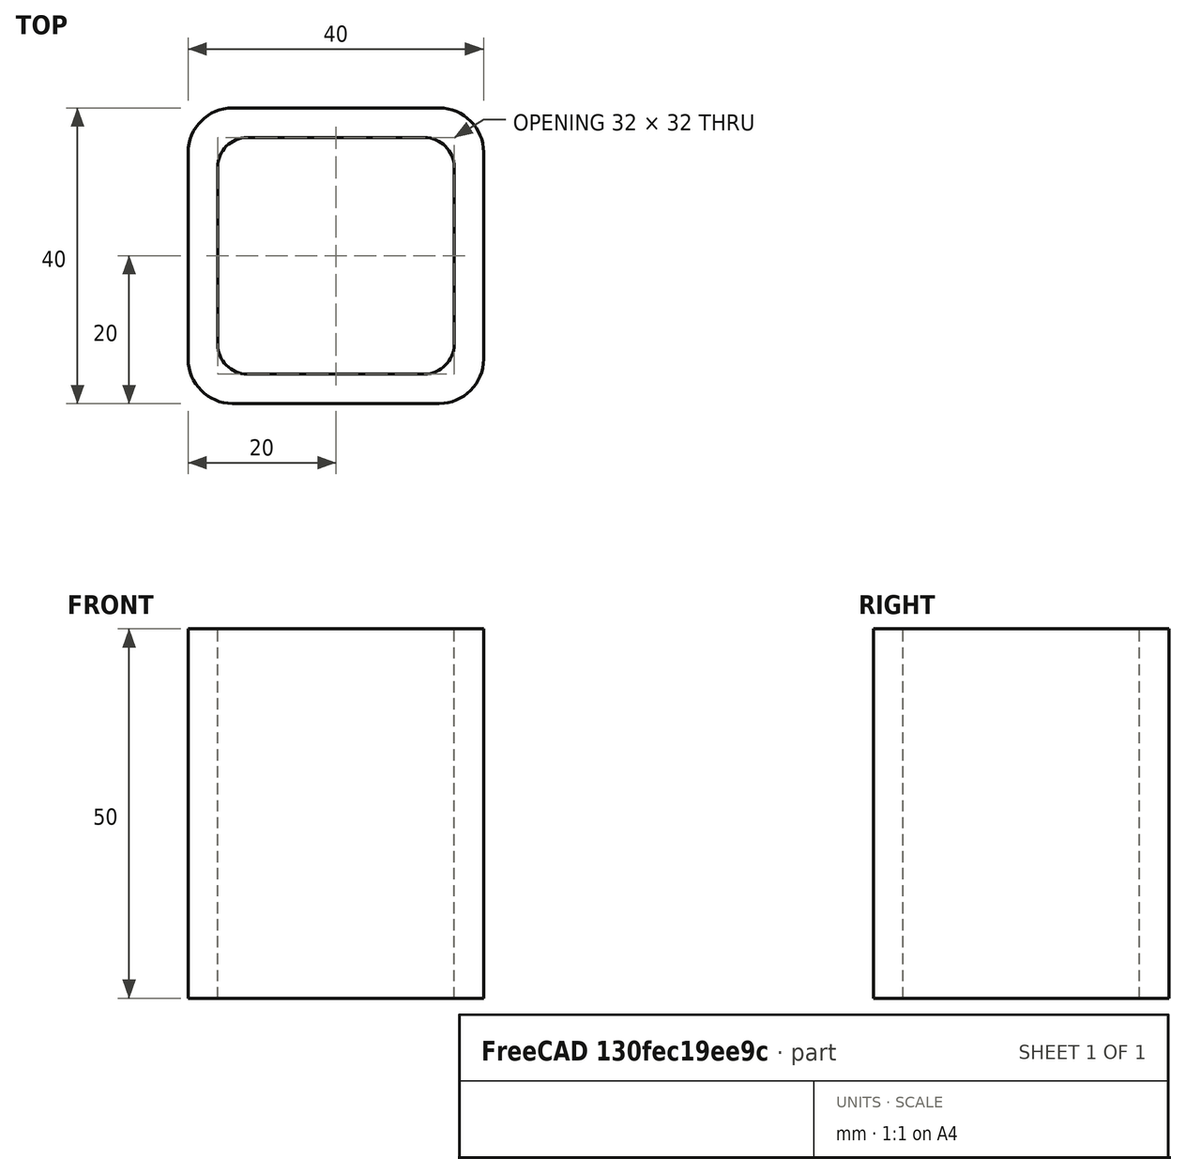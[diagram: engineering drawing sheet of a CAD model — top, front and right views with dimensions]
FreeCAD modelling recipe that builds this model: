
FCSTD DOCUMENT  (FreeCAD 0.15R4671 (Git))
Label: Square hollow section 40x40x4 EN10219 S235JRH
License: All rights reserved
LicenseURL: http://en.wikipedia.org/wiki/All_rights_reserved
objects: Sketcher::SketchObject×1, Part::Extrusion×1
note: 2 computed .brp shape members not serialized (recipe doc carries the construction recipe); baked Part::Feature solids carry a one-line shape summary decoded from their .brp

FEATURE [Sketcher::SketchObject] Sketch
  sketch-geometry (16):
    g0: LineSegment StartX=-12 StartY=16 StartZ=0 EndX=12 EndY=16 EndZ=0
    g1: LineSegment StartX=16 StartY=12 StartZ=0 EndX=16 EndY=-12 EndZ=0
    g2: LineSegment StartX=12 StartY=-16 StartZ=0 EndX=-12 EndY=-16 EndZ=0
    g3: LineSegment StartX=-16 StartY=-12 StartZ=0 EndX=-16 EndY=12 EndZ=0
    g4: LineSegment StartX=-14 StartY=20 StartZ=0 EndX=14 EndY=20 EndZ=0
    g5: LineSegment StartX=20 StartY=14 StartZ=0 EndX=20 EndY=-14 EndZ=0
    g6: LineSegment StartX=14 StartY=-20 StartZ=0 EndX=-14 EndY=-20 EndZ=0
    g7: LineSegment StartX=-20 StartY=-14 StartZ=0 EndX=-20 EndY=14 EndZ=0
    g8: ArcOfCircle CenterX=-12 CenterY=12 CenterZ=0 NormalX=0 NormalY=0 NormalZ=1 Radius=4 StartAngle=1.5708 EndAngle=3.14159
    g9: ArcOfCircle CenterX=12 CenterY=12 CenterZ=0 NormalX=0 NormalY=0 NormalZ=1 Radius=4 StartAngle=0 EndAngle=1.5708
    g10: ArcOfCircle CenterX=12 CenterY=-12 CenterZ=0 NormalX=0 NormalY=0 NormalZ=1 Radius=4 StartAngle=4.71239 EndAngle=6.28319
    g11: ArcOfCircle CenterX=-12 CenterY=-12 CenterZ=0 NormalX=0 NormalY=0 NormalZ=1 Radius=4 StartAngle=3.14159 EndAngle=4.71239
    g12: ArcOfCircle CenterX=14 CenterY=14 CenterZ=0 NormalX=0 NormalY=0 NormalZ=1 Radius=6 StartAngle=0 EndAngle=1.5708
    g13: ArcOfCircle CenterX=14 CenterY=-14 CenterZ=0 NormalX=0 NormalY=0 NormalZ=1 Radius=6 StartAngle=4.71239 EndAngle=6.28319
    g14: ArcOfCircle CenterX=-14 CenterY=-14 CenterZ=0 NormalX=0 NormalY=0 NormalZ=1 Radius=6 StartAngle=3.14159 EndAngle=4.71239
    g15: ArcOfCircle CenterX=-14 CenterY=14 CenterZ=0 NormalX=0 NormalY=0 NormalZ=1 Radius=6 StartAngle=1.5708 EndAngle=3.14159
  constraints (36):
    c: Horizontal(g2)
    c: Vertical(g3)
    c: Horizontal(g6)
    c: Vertical(g7)
    c: Tangent(g3,g8) = 1.5708
    c: Tangent(g0,g8) = 1.5708
    c: Tangent(g0,g9) = 1.5708
    c: Tangent(g1,g9) = 1.5708
    c: Tangent(g1,g10) = 1.5708
    c: Tangent(g2,g10) = 1.5708
    c: Tangent(g2,g11) = 1.5708
    c: Tangent(g3,g11) = 1.5708
    c: Tangent(g4,g12) = 1.5708
    c: Tangent(g5,g12) = 1.5708
    c: Tangent(g5,g13) = 1.5708
    c: Tangent(g6,g13) = 1.5708
    c: Tangent(g6,g14) = 1.5708
    c: Tangent(g7,g14) = 1.5708
    c: Tangent(g7,g15) = 1.5708
    c: Tangent(g4,g15) = 1.5708
    c: Equal(g9,g8)
    c: Equal(g9,g11)
    c: Equal(g9,g10)
    c: Equal(g12,g15)
    c: Equal(g12,g14)
    c: Equal(g12,g13)
    c: Symmetric(g4,g6,g-1)
    c: Symmetric(g7,g5,g-2)
    c: DistanceY(g4,g6) = -40
    c: DistanceX(g7,g5) = 40
    c: Symmetric(g3,g1,g-2)
    c: Symmetric(g0,g2,g-1)
    c: DistanceY(g0,g4) = 4
    c: DistanceX(g5,g1) = -4
    c: Radius(g9) = 4
    c: Radius(g12) = 6
FEATURE [Part::Extrusion] Extrude  label="Square hollow section 40x40x4 EN10219 S235JRH"
  Base = -> Sketch
  Dir = (0,0,50)
  Solid = true
